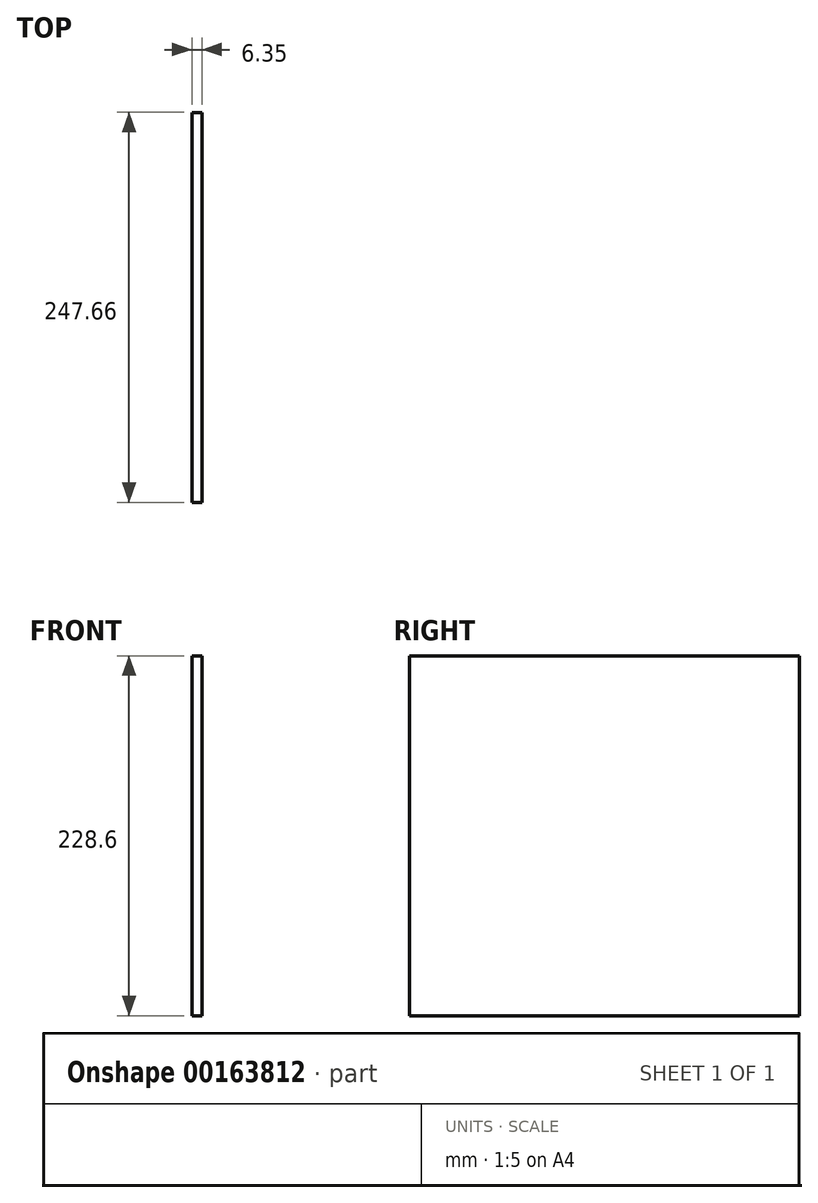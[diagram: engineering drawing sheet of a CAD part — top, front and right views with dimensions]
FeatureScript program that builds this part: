
annotation { "Feature Type Name" : "Feature", "Feature Type Description" : "" }
export const myFeature = defineFeature(function(context is Context, id is Id, definition is map)
    precondition{}
    {
        {
            var Q0;
            Q0=qCreatedBy(makeId("Right.planeOp"),FACE);
            var sketch = newSketch(context, id + "F0", { "sketchPlane" : qUnion([Q0])});
            skLineSegment(sketch, "E0.bottom", {"start": v(123.83, -114.3) * mm, "end": v(-123.83, -114.3) * mm});
            skLineSegment(sketch, "E0.top", {"start": v(123.83, 114.3) * mm, "end": v(-123.83, 114.3) * mm});
            skLineSegment(sketch, "E0.left", {"start": v(123.83, -114.3) * mm, "end": v(123.83, 114.3) * mm});
            skLineSegment(sketch, "E0.right", {"start": v(-123.83, -114.3) * mm, "end": v(-123.83, 114.3) * mm});
            skPoint(sketch, "E0.middle", {"position": v(0, 0) * mm});
            skSolve(sketch);
        }
        {
            var Q0;
            Q0 = qSketchRegion(id + "F0", true);
            extrude(context, id + "F1", {"entities" : qUnion([Q0]), "depth" : 6.35 * mm});
        }
    });
